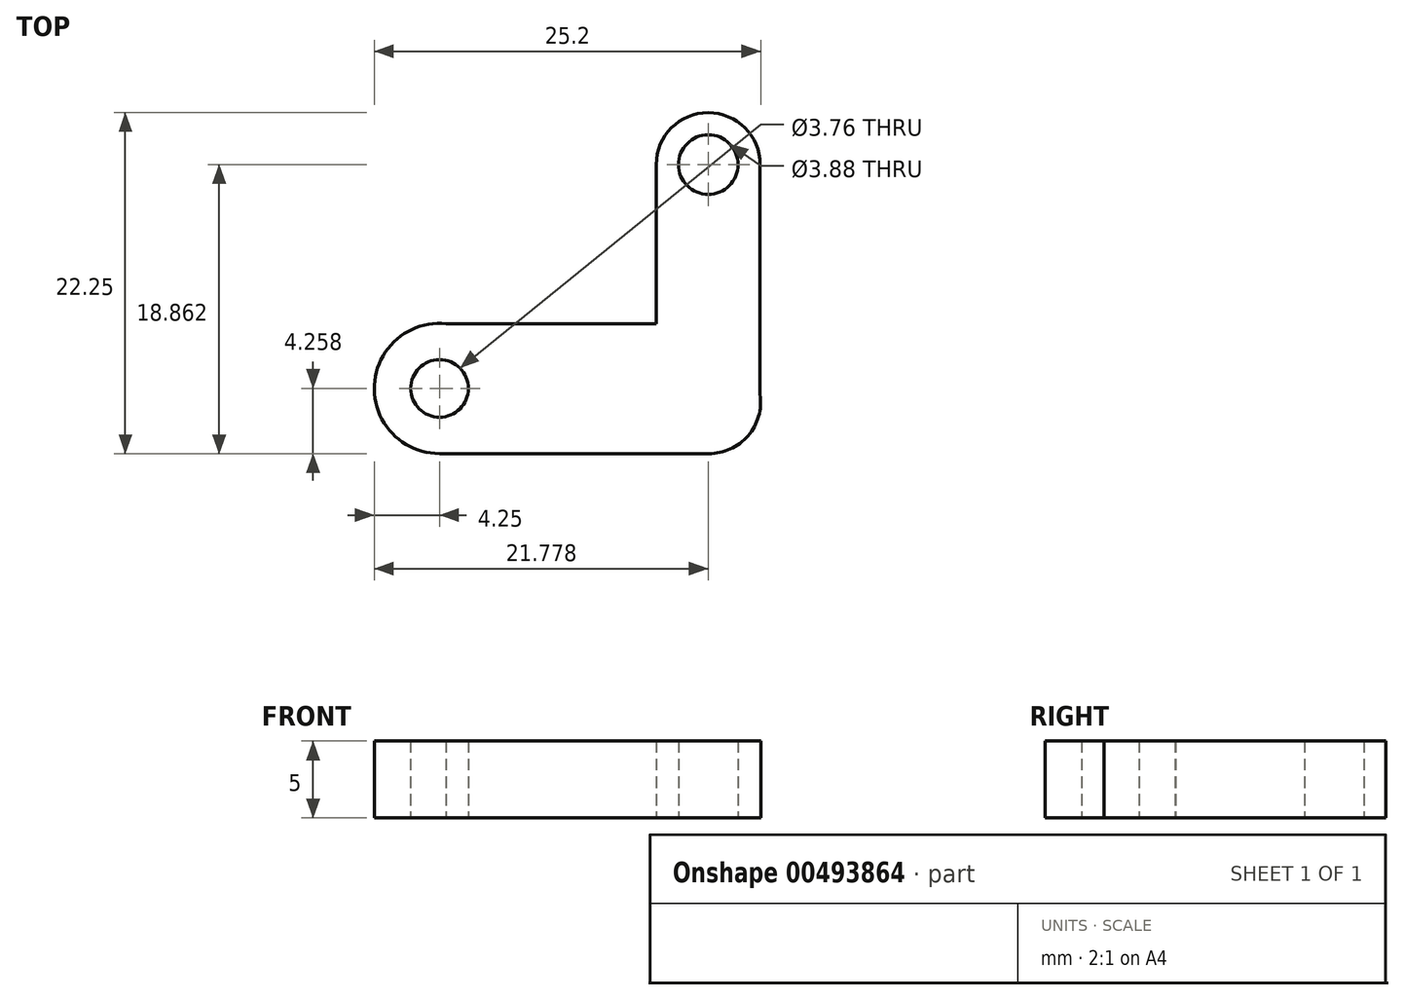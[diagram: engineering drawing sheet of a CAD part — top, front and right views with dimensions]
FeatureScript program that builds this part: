
annotation { "Feature Type Name" : "Feature", "Feature Type Description" : "" }
export const myFeature = defineFeature(function(context is Context, id is Id, definition is map)
    precondition{}
    {
        {
            var Q0;
            Q0=qCreatedBy(makeId("Top.planeOp"),FACE);
            var sketch = newSketch(context, id + "F0", { "sketchPlane" : qUnion([Q0])});
            skLineSegment(sketch, "E0", {"start": v(-10.57, 0.94) * mm, "end": v(7, 0.94) * mm});
            skArc(sketch, "E1", {"start": v(7, 0.94) * mm, "mid": v(9.55, 2.1) * mm, "end": v(10.34, 4.8) * mm});
            skLineSegment(sketch, "E2", {"start": v(10.34, 4.8) * mm, "end": v(10.34, 19.8) * mm});
            skArc(sketch, "E3", {"start": v(10.34, 19.8) * mm, "mid": v(6.96, 23.19) * mm, "end": v(3.57, 19.8) * mm});
            skFitSpline(sketch, "E4", {"points": [v(3.57, 9.43) * mm, v(3.57, 19.8) * mm], "startDerivative": vector(0, 10.37) * mm, "endDerivative": vector(0, 10.37) * mm});
            skFitSpline(sketch, "E5", {"points": [v(3.83, 19.63) * mm, v(3.57, 19.8) * mm], "startDerivative": vector(-0.26, 0.17) * mm, "endDerivative": vector(-0.26, 0.17) * mm});
            skFitSpline(sketch, "E6", {"points": [v(-10.14, 9.43) * mm, v(3.57, 9.43) * mm], "startDerivative": vector(13.71, 0) * mm, "endDerivative": vector(13.71, 0) * mm});
            skArc(sketch, "E7", {"start": v(-10.14, 9.43) * mm, "mid": v(-14.82, 5.41) * mm, "end": v(-10.57, 0.94) * mm});
            skCircle(sketch, "E8", {"center": v(6.96, 19.8) * mm, "radius": 1.94 * mm});
            skCircle(sketch, "E9", {"center": v(-10.57, 5.2) * mm, "radius": 1.88 * mm});
            skSolve(sketch);
        }
        {
            var Q0;
            Q0=makeQuery(id+"F0.imprint","IMPRINT",FACE,{"disambiguationData":[TD([[makeQuery(id+"F0.imprint","IMPRINT",EDGE,{"derivedFrom":sQuery(id+"F0.wireOp",EDGE,"E0")}),1.0]])]});
            extrude(context, id + "F1", {"entities" : qUnion([Q0]), "depth" : 5 * mm});
        }
    });
